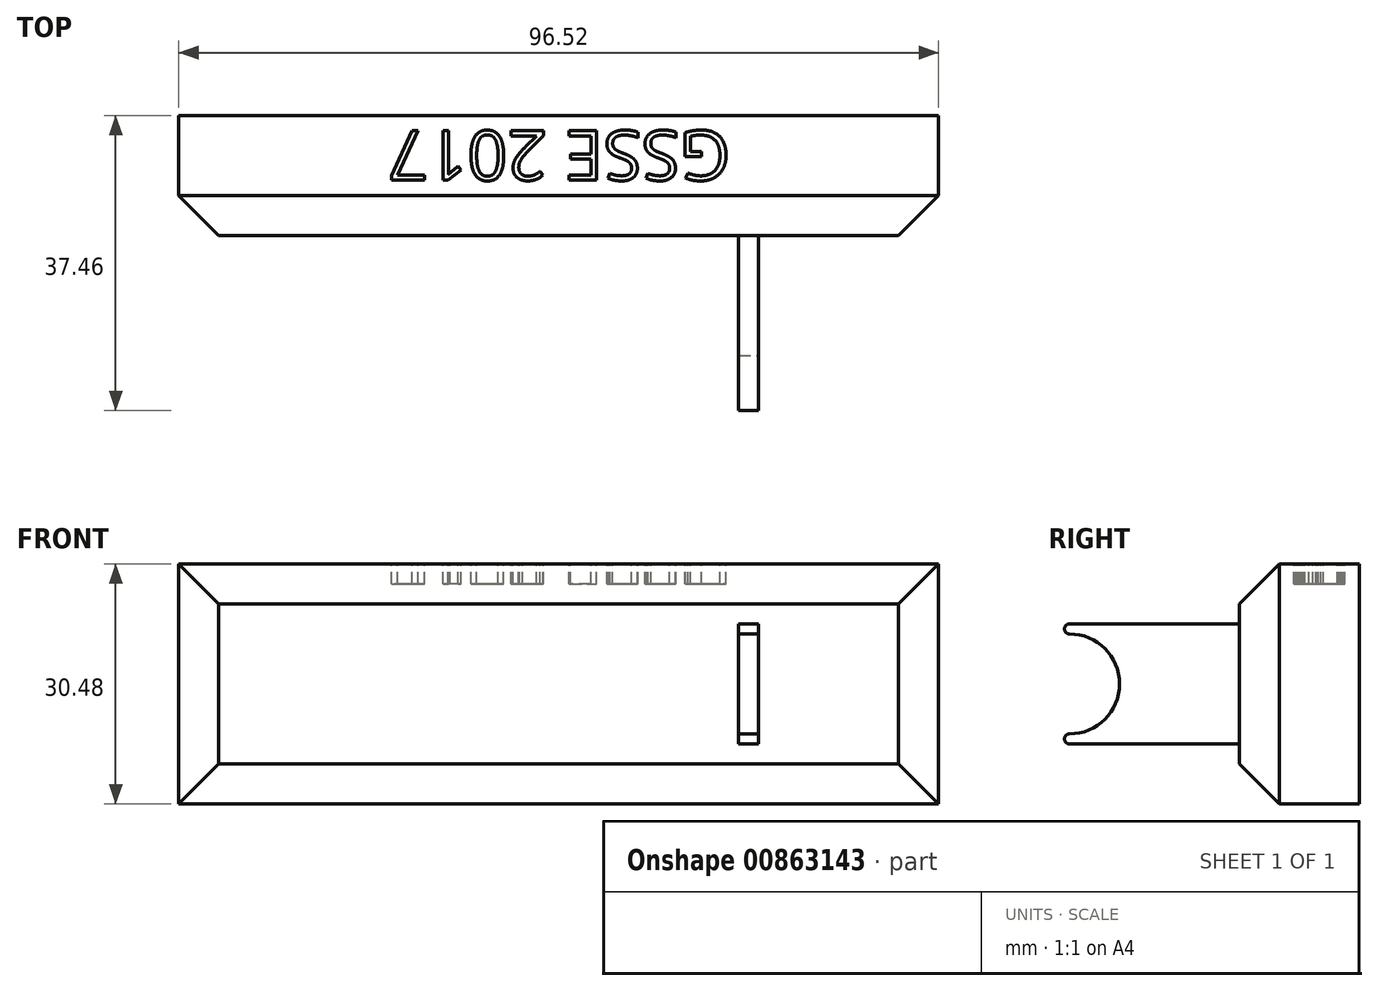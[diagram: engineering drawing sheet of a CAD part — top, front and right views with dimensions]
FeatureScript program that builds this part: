
annotation { "Feature Type Name" : "Feature", "Feature Type Description" : "" }
export const myFeature = defineFeature(function(context is Context, id is Id, definition is map)
    precondition{}
    {
        {
            var Q0;
            Q0=qCreatedBy(makeId("Front.planeOp"),FACE);
            var sketch = newSketch(context, id + "F0", { "sketchPlane" : qUnion([Q0])});
            skLineSegment(sketch, "E0.bottom", {"start": v(48.26, -15.24) * mm, "end": v(-48.26, -15.24) * mm});
            skLineSegment(sketch, "E0.top", {"start": v(48.26, 15.24) * mm, "end": v(-48.26, 15.24) * mm});
            skLineSegment(sketch, "E0.left", {"start": v(48.26, -15.24) * mm, "end": v(48.26, 15.24) * mm});
            skLineSegment(sketch, "E0.right", {"start": v(-48.26, -15.24) * mm, "end": v(-48.26, 15.24) * mm});
            skPoint(sketch, "E0.middle", {"position": v(0, 0) * mm});
            skSolve(sketch);
        }
        {
            var Q0;
            Q0=makeQuery(id+"F0.imprint","IMPRINT",FACE,{"disambiguationData":[TD([[makeQuery(id+"F0.imprint","IMPRINT",EDGE,{"derivedFrom":sQuery(id+"F0.wireOp",EDGE,"E0.bottom")}),-1.0]])]});
            extrude(context, id + "F1", {"entities" : qUnion([Q0]), "depth" : 15.24 * mm, "offsetDistance" : 25.4 * mm});
        }
        {
            var Q0;
            Q0=makeQuery(id+"F1.opExtrude","CAP_EDGE",EDGE,{"disambiguationData":[OSD([sQuery(id+"F0.wireOp",EDGE,"E0.right")])],"isStart":false});
            var Q1;
            Q1=makeQuery(id+"F1.opExtrude","CAP_EDGE",EDGE,{"disambiguationData":[OSD([sQuery(id+"F0.wireOp",EDGE,"E0.top")])],"isStart":false});
            var Q2;
            Q2=makeQuery(id+"F1.opExtrude","CAP_EDGE",EDGE,{"disambiguationData":[OSD([sQuery(id+"F0.wireOp",EDGE,"E0.bottom")])],"isStart":false});
            var Q3;
            Q3=makeQuery(id+"F1.opExtrude","CAP_EDGE",EDGE,{"disambiguationData":[OSD([sQuery(id+"F0.wireOp",EDGE,"E0.left")])],"isStart":false});
            chamfer(context, id + "F2", {"entities" : qUnion([Q0, Q1, Q2, Q3]), "width" : 5.08 * mm, "tangentPropagation" : true});
        }
        {
            var Q0;
            Q0=makeQuery(id+"F1.opExtrude","SWEPT_FACE",FACE,{"disambiguationData":[OSD([sQuery(id+"F0.wireOp",EDGE,"E0.left")])]});
            cPlane(context, id + "F3", {"entities" : qUnion([Q0]), "cplaneType" : CPlaneType.OFFSET, "offset" : 22.86 * mm, "oppositeDirection" : true, "width" : 152.4 * mm, "height" : 152.4 * mm});
        }
        {
            var Q0;
            Q0=qCreatedBy(id+"F3.planeOp",FACE);
            var sketch = newSketch(context, id + "F4", { "sketchPlane" : qUnion([Q0])});
            skLineSegment(sketch, "E1.bottom", {"start": v(-15.24, 7.62) * mm, "end": v(-33.02, 7.62) * mm});
            skLineSegment(sketch, "E1.top", {"start": v(-15.24, -7.62) * mm, "end": v(-33.02, -7.62) * mm});
            skLineSegment(sketch, "E1.left", {"start": v(-15.24, 7.62) * mm, "end": v(-15.24, -7.62) * mm});
            skLineSegment(sketch, "E1.right", {"start": v(-33.02, 7.62) * mm, "end": v(-33.02, -7.62) * mm});
            skPoint(sketch, "E1.middle", {"position": v(-24.13, 0) * mm});
            skLineSegment(sketch, "E2", {"start": v(-33.02, -7.62) * mm, "end": v(-36.83, -7.62) * mm});
            skLineSegment(sketch, "E3", {"start": v(-33.02, 7.62) * mm, "end": v(-36.83, 7.62) * mm});
            skCircle(sketch, "E4", {"center": v(-36.83, -6.99) * mm, "radius": 0.64 * mm});
            skCircle(sketch, "E5", {"center": v(-36.83, 6.99) * mm, "radius": 0.64 * mm});
            skLineSegment(sketch, "E6", {"start": v(-36.83, -6.99) * mm, "end": v(-36.83, -6.35) * mm});
            skLineSegment(sketch, "E7", {"start": v(-36.83, 6.99) * mm, "end": v(-36.83, 6.35) * mm});
            skArc(sketch, "E8", {"start": v(-36.83, -6.35) * mm, "mid": v(-30.48, 0) * mm, "end": v(-36.83, 6.35) * mm});
            skSolve(sketch);
        }
        {
            var Q0;
            Q0=makeQuery(id+"F4.imprint","IMPRINT",FACE,{"disambiguationData":[TD([[makeQuery(id+"F4.imprint","IMPRINT",EDGE,{"derivedFrom":sQuery(id+"F4.wireOp",EDGE,"E1.bottom")}),1.0]])]});
            var Q1;
            {var subQ0=sQuery(id+"F4.wireOp",EDGE,"E4");var subQ1=makeQuery(id+"F4.imprint","INTERSECT",VERTEX,{"derivedFrom":[sQuery(id+"F4.wireOp",EDGE,"E2"),subQ0]});Q1=makeQuery(id+"F4.imprint","IMPRINT",FACE,{"disambiguationData":[TD([[makeQuery(id+"F4.imprint","IMPRINT",EDGE,{"disambiguationData":[TD([[subQ1,1.0]])],"derivedFrom":subQ0}),1.0]])]});}
            var Q2;
            {var subQ0=sQuery(id+"F4.wireOp",EDGE,"E2");Q2=makeQuery(id+"F4.imprint","IMPRINT",FACE,{"disambiguationData":[TD([[makeQuery(id+"F4.imprint","IMPRINT",EDGE,{"derivedFrom":subQ0}),-1.0]])]});}
            var Q3;
            {var subQ0=sQuery(id+"F4.wireOp",EDGE,"E5");var subQ1=makeQuery(id+"F4.imprint","INTERSECT",VERTEX,{"derivedFrom":[sQuery(id+"F4.wireOp",EDGE,"E3"),subQ0]});Q3=makeQuery(id+"F4.imprint","IMPRINT",FACE,{"disambiguationData":[TD([[makeQuery(id+"F4.imprint","IMPRINT",EDGE,{"disambiguationData":[TD([[subQ1,-1.0]])],"derivedFrom":subQ0}),1.0]])]});}
            var Q4;
            {var subQ0=sQuery(id+"F4.wireOp",EDGE,"E3");Q4=makeQuery(id+"F4.imprint","IMPRINT",FACE,{"disambiguationData":[TD([[makeQuery(id+"F4.imprint","IMPRINT",EDGE,{"derivedFrom":subQ0}),1.0]])]});}
            extrude(context, id + "F5", {"entities" : qUnion([Q0, Q1, Q2, Q3, Q4]), "operationType" : NewBodyOperationType.ADD, "oppositeDirection" : true, "depth" : 2.54 * mm, "offsetDistance" : 25.4 * mm});
        }
        {
            var Q0;
            Q0=makeQuery(id+"F1.opExtrude","SWEPT_FACE",FACE,{"disambiguationData":[OSD([sQuery(id+"F0.wireOp",EDGE,"E0.left")])]});
            cPlane(context, id + "F6", {"entities" : qUnion([Q0]), "cplaneType" : CPlaneType.OFFSET, "offset" : 49.53 * mm, "oppositeDirection" : true, "width" : 152.4 * mm, "height" : 152.4 * mm});
        }
        {
            var Q0;
            Q0=makeQuery(id+"F1.opExtrude","SWEPT_FACE",FACE,{"disambiguationData":[OSD([sQuery(id+"F0.wireOp",EDGE,"E0.top")])]});
            var sketch = newSketch(context, id + "F7", { "sketchPlane" : qUnion([Q0])});
            skText(sketch, "E9", { "text": "GSSE 2017\n", "fontName": "OpenSans-Regular.ttf"});
            const initialGuessF7  = {"E9": [0.0218, -0.00192, -1, 0, 0.00635]};
            skSetInitialGuess(sketch, initialGuessF7);
            skSolve(sketch);
        }
        {
            var Q0;
            Q0 = qSketchRegion(id + "F7", true);
            extrude(context, id + "F8", {"entities" : qUnion([Q0]), "operationType" : NewBodyOperationType.REMOVE, "oppositeDirection" : true, "depth" : 2.54 * mm, "offsetDistance" : 25.4 * mm});
        }
    });
